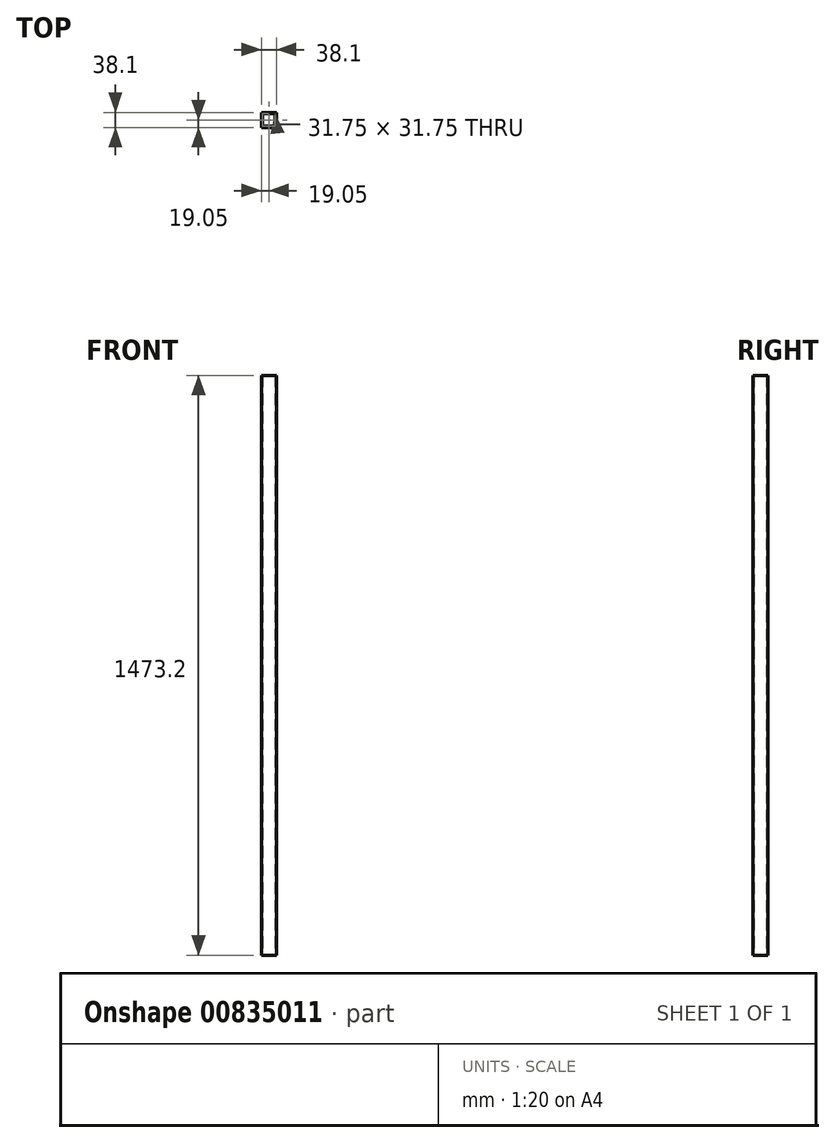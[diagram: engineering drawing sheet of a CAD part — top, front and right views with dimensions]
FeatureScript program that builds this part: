
annotation { "Feature Type Name" : "Feature", "Feature Type Description" : "" }
export const myFeature = defineFeature(function(context is Context, id is Id, definition is map)
    precondition{}
    {
        {
            var Q0;
            Q0=qCreatedBy(makeId("Top.planeOp"),FACE);
            var sketch = newSketch(context, id + "F0", { "sketchPlane" : qUnion([Q0])});
            skLineSegment(sketch, "E0.bottom", {"start": v(19.05, 19.05) * mm, "end": v(-19.05, 19.05) * mm});
            skLineSegment(sketch, "E0.top", {"start": v(19.05, -19.05) * mm, "end": v(-19.05, -19.05) * mm});
            skLineSegment(sketch, "E0.left", {"start": v(19.05, 19.05) * mm, "end": v(19.05, -19.05) * mm});
            skLineSegment(sketch, "E0.right", {"start": v(-19.05, 19.05) * mm, "end": v(-19.05, -19.05) * mm});
            skPoint(sketch, "E0.middle", {"position": v(0, 0) * mm});
            skLineSegment(sketch, "E1.bottom", {"start": v(15.88, 15.88) * mm, "end": v(-15.88, 15.88) * mm});
            skLineSegment(sketch, "E1.top", {"start": v(15.88, -15.88) * mm, "end": v(-15.87, -15.88) * mm});
            skLineSegment(sketch, "E1.left", {"start": v(15.87, 15.88) * mm, "end": v(15.88, -15.88) * mm});
            skLineSegment(sketch, "E1.right", {"start": v(-15.88, 15.88) * mm, "end": v(-15.87, -15.88) * mm});
            skSolve(sketch);
        }
        {
            var Q0;
            Q0 = qSketchRegion(id + "F0", true);
            extrude(context, id + "F1", {"entities" : qUnion([Q0]), "endBound" : BoundingType.SYMMETRIC, "depth" : 1473.2 * mm, "offsetDistance" : 25.4 * mm});
        }
    });
